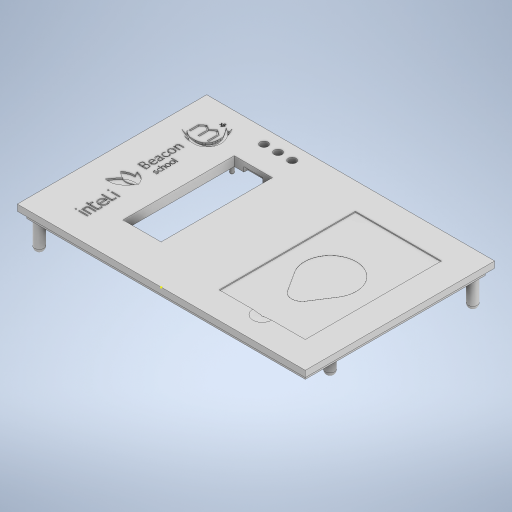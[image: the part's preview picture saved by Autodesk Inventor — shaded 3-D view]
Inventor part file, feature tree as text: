
AUTODESK INVENTOR PART (.ipt)
format: ipt  version: 2023 (Build 270158000, 158)  size: 2,711,040 bytes
history: native  units: mm
features: extrude x27, sketch x12, other x4, fillet x2
ambient origin geometry x8: Origin, YZ Plane, XZ Plane, XY Plane, X Axis, Y Axis, Z Axis, Center Point
bodies: Body1 (feature_tree)
feature tree (45):
  other  "Sólido1"
  sketch  "Esboço1"  dims[d0=184.0mm d1=121.0mm]
  extrude  "Base"  Depth=121.0mm
  extrude  "Área do Cartão"  Depth=55.0mm
  extrude  "Área da Tag"  Depth=13.0mm
  extrude  "Suporte Cartão"  Depth=71.15mm
  extrude  "Logo INTELI"  Depth=8.0mm TaperAngle=0.0deg
  extrude  "Logo BEACON"  Depth=12.0mm
  extrude  "Logo IOBEE 1"  Depth=1.0mm TaperAngle=0.0deg
  extrude  "Logo IOBEE 2"  Depth=1.0mm TaperAngle=0.0deg
  extrude  "Logo IOBEE 3"  Depth=1.0mm TaperAngle=0.0deg
  other  "Perfil LCD"
  extrude  "LCD Pinos de trás"  Depth=79.9mm
  extrude  "LCD Chaveta de trás"  Depth=40.0mm
  extrude  "LCD Alocamento"  Depth=6.0mm TaperAngle=0.0deg
  extrude  "LCD Pinos Guia"  Depth=6.0mm
  extrude  "Rasgo de Encaixe"  Depth=6.0mm
  other  "Perfil ESP32"
  extrude  "Alocamento ESP32"  Depth=5.0mm TaperAngle=0.0deg
  extrude  "ESP32 Wi-Fi"  Depth=2.0mm TaperAngle=0.0deg
  extrude  "Rasgo Protoboard"  Depth=7.0mm TaperAngle=0.0deg
  extrude  "RFID"  Depth=4.0mm TaperAngle=0.0deg
  extrude  "RFID Cabeamento"  Depth=19.0mm
  extrude  "Furo Leds"  Depth=28.0mm
  extrude  "Rasgo Fios"  Depth=8.0mm
  other  "Perfil Leds GND"
  extrude  "GND Leds"  Depth=5.0mm TaperAngle=0.0deg
  extrude  "GND Leds 2"  Depth=3.0mm TaperAngle=0.0deg
  extrude  "Fios GND"  Depth=4.5mm
  extrude  "Rasgo RFID-ESP"  Depth=5.0mm TaperAngle=0.0deg
  extrude  "Pinos de Encaixe"  Depth=4.5mm
  fillet  "Arredondamento-  Pinos de Encaixe"  Radius=60.0mm
  fillet  "Arredondamento- Pinos Guia LCD"  Radius=6.0mm
  extrude  "Entrada USB-C ESP32"  Depth=4.5mm
  sketch  "Esboço30"  dims[d48=6.2mm d49=6.0mm d50=0.0mm d51=6.0mm d52=6.0mm d53=5.0mm d54=0.0mm d55=2.0mm d56=0.0mm d69=7.0mm d70=0.0mm d72=4.0mm d73=0.0mm d111=19.0mm d112=28.0mm d113=8.0mm d114=5.0mm d115=0.0mm d116=3.0mm d117=0.0mm d120=164.0mm d122=5.0mm d123=0.0mm d130=39.4mm d131=60.0mm d132=6.0mm d133=0.0mm d136=20.4mm d138=3.0mm d139=0.0mm d140=5.0mm d141=5.0mm d142=5.0mm d143=9.0mm d145=9.0mm d149=18.0mm d151=11.469816mm d152=0.0mm d153=0.0mm d158=2.0mm d159=0.0mm d162=2.0mm d163=0.0mm d166=10.0mm d167=2.8mm d168=2.0mm d169=0.0mm d170=13.0mm d171=2.0mm d172=0.0mm d173=2.0mm d174=0.0mm d177=6.0mm d180=6.0mm d183=6.0mm d184=6.0mm d185=18.0mm d186=0.0mm d191=3.0mm d196=1.0mm d197=60.0mm d199=0.0mm d200=0.0mm d201=2.5mm d202=75.9mm d203=32.05mm d209=178.0mm d210=115.0mm d211=4.5mm d57=0.5mm d58=0.872665mm d59=0.5mm d60=0.872665mm d86=0.872665mm d87=0.872665mm d124=0.5mm d125=0.872665mm d175=0.5mm d176=0.872665mm]
  sketch  "Esboço3"  dims[d2=55.0mm d3=87.0mm]
  sketch  "Esboço4"  dims[d5=17.0mm d8=13.0mm]
  sketch  "Esboço12"  dims[d9=24.36mm d10=71.15mm]
  sketch  "Esboço18"  dims[d24=8.0mm d25=0.0mm d26=0.6mm d27=0.0mm]
  sketch  "Esboço19"  dims[d28=0.7mm d29=0.0mm d30=12.0mm]
  sketch  "Esboço21"  dims[d31=0.6mm d32=-14.660766mm d33=1.0mm d34=0.0mm]
  sketch  "Esboço24"  dims[d35=1.0mm d36=0.0mm d37=0.5mm d38=0.0mm]
  sketch  "Esboço25"  dims[d39=1.0mm d40=0.0mm d41=1.2mm d42=0.0mm]
  sketch  "Esboço26"  dims[d43=36.05mm d44=79.9mm]
  sketch  "Esboço29"  dims[d45=4.0mm d47=40.0mm]
